# Revit family: HVAC_Other_Airzone_Main-Control-Board1
name_source: partatom
category: Mechanical Equipment
revit_build: Autodesk Revit 2016 (Build: 20161004_0715(x64)
units: mm (PartAtom-declared; Revit-internal decimal feet)

## family parameters
Cut with Voids When Loaded = No
Host = Face
OmniClass Number = 23.85.80.11.24
OmniClass Title = Environmental Controls
Part Type = Normal
Room Calculation Point = No
Round Connector Dimension = Use Diameter
Shared = No

## types (1)
- Generic
    Apparent Load = 25 VA
    Default Elevation = 900 mm
    Description = Main Control Board
    Disclaimer = All information provided in this model is reviewed before being published. However, Airzone cannot guarantee this model is error-free, therefore users are strongly encouraged to check for technical documentation and updates
    Fixing = Surface through support
    Long Description = Electronic board that controls the system through wired and wireless devices. Wall mounted.
    Main Material = Plastic - AIRZONE - Smooth - Off-white
    Manufacturer = AIRZONE
    Model = AZXX6MAINBOARD
    Product Code = AZXX6MAINBOARD
    Product Comments = Refer to technical documentation for further details
    Product Documentation Download URL = http://doc.airzone.es
    Protection Class = IP 20
    Revit Model Version = 1.0
    Type Image Comments = Image available in product documentation download
    URL = www.airzone.es
    Voltage = 230 V

## geometry (parser evidence)
native form markers: Sweep x5
no freeform markers — native parametric forms only
